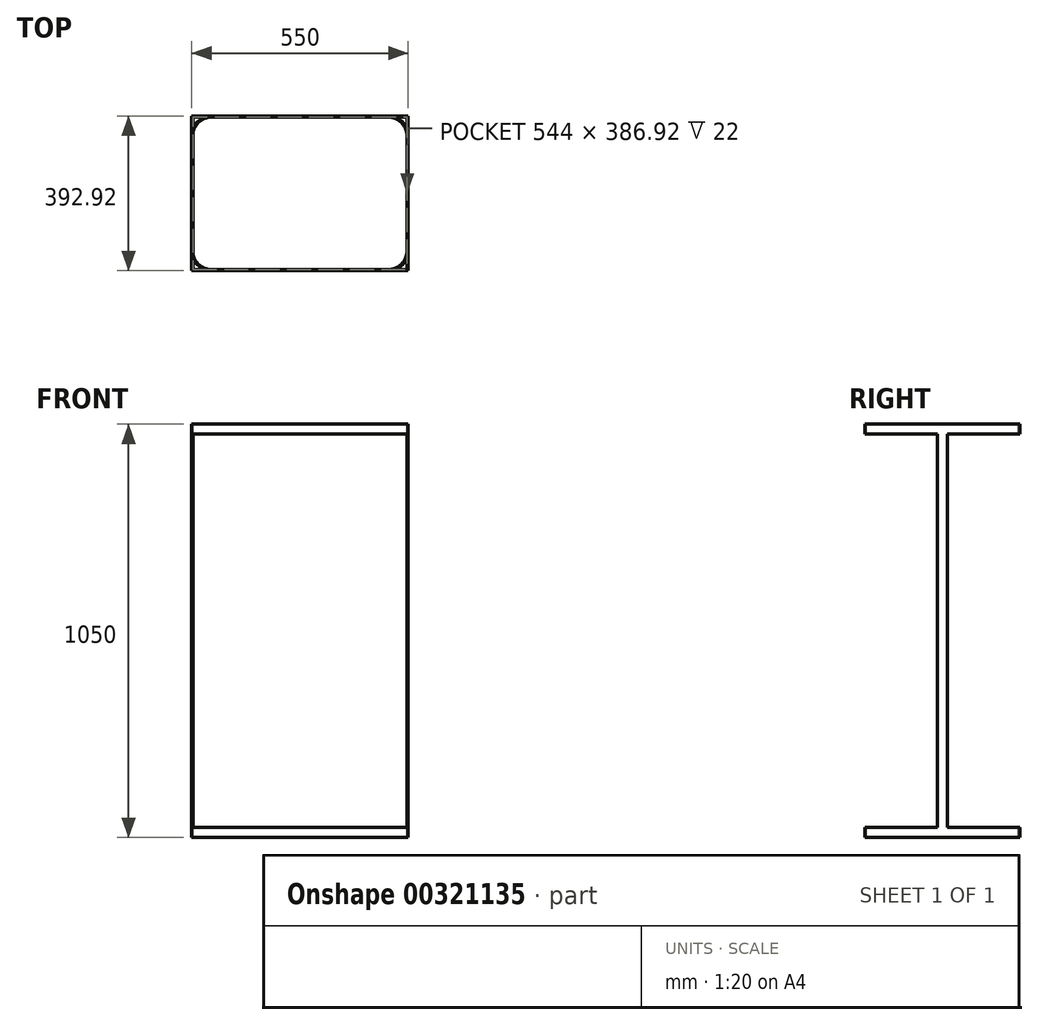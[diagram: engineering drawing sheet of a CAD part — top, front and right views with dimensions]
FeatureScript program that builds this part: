
annotation { "Feature Type Name" : "Feature", "Feature Type Description" : "" }
export const myFeature = defineFeature(function(context is Context, id is Id, definition is map)
    precondition{}
    {
        {
            var Q0;
            Q0=qCreatedBy(makeId("Top.planeOp"),FACE);
            var sketch = newSketch(context, id + "F0", { "sketchPlane" : qUnion([Q0])});
            skLineSegment(sketch, "E0", {"start": v(-225, -20) * mm, "end": v(225, -20) * mm});
            skLineSegment(sketch, "E1", {"start": v(-225, -412.92) * mm, "end": v(225, -412.92) * mm});
            skLineSegment(sketch, "E2", {"start": v(275, -70) * mm, "end": v(275, -362.92) * mm});
            skLineSegment(sketch, "E3", {"start": v(-275, -70) * mm, "end": v(-275, -362.92) * mm});
            skArc(sketch, "E4", {"start": v(-225, -20) * mm, "mid": v(-260.36, -34.64) * mm, "end": v(-275, -70) * mm});
            skArc(sketch, "E5", {"start": v(-275, -362.92) * mm, "mid": v(-260.36, -398.28) * mm, "end": v(-225, -412.92) * mm});
            skArc(sketch, "E6", {"start": v(225, -412.92) * mm, "mid": v(260.36, -398.28) * mm, "end": v(275, -362.92) * mm});
            skArc(sketch, "E7", {"start": v(275, -70) * mm, "mid": v(260.36, -34.64) * mm, "end": v(225, -20) * mm});
            skArc(sketch, "E8.0", {"start": v(-225, -23) * mm, "mid": v(-258.23, -36.77) * mm, "end": v(-272, -70) * mm});
            skLineSegment(sketch, "E8.1", {"start": v(-272, -70) * mm, "end": v(-272, -362.92) * mm});
            skLineSegment(sketch, "E8.2", {"start": v(-225, -23) * mm, "end": v(225, -23) * mm});
            skArc(sketch, "E8.3", {"start": v(-272, -362.92) * mm, "mid": v(-258.23, -396.15) * mm, "end": v(-225, -409.92) * mm});
            skArc(sketch, "E8.4", {"start": v(272, -70) * mm, "mid": v(258.23, -36.77) * mm, "end": v(225, -23) * mm});
            skLineSegment(sketch, "E8.5", {"start": v(272, -70) * mm, "end": v(272, -362.92) * mm});
            skArc(sketch, "E8.6", {"start": v(225, -409.92) * mm, "mid": v(258.23, -396.15) * mm, "end": v(272, -362.92) * mm});
            skLineSegment(sketch, "E8.7", {"start": v(-225, -409.92) * mm, "end": v(225, -409.92) * mm});
            skSolve(sketch);
        }
        {
            var Q0;
            Q0 = qSketchRegion(id + "F0", true);
            extrude(context, id + "F1", {"entities" : qUnion([Q0]), "oppositeDirection" : true, "depth" : 25 * mm});
        }
        {
            var Q0;
            Q0=makeQuery(id+"F1.opExtrude","SWEPT_FACE",FACE,{"disambiguationData":[OSD([sQuery(id+"F0.wireOp",EDGE,"E2")])]});
            var sketch = newSketch(context, id + "F2", { "sketchPlane" : qUnion([Q0])});
            skLineSegment(sketch, "E9.bottom", {"start": v(-228.96, -25) * mm, "end": v(-203.96, -25) * mm});
            skLineSegment(sketch, "E9.top", {"start": v(-228.96, -1025) * mm, "end": v(-203.96, -1025) * mm});
            skLineSegment(sketch, "E9.left", {"start": v(-228.96, -25) * mm, "end": v(-228.96, -1025) * mm});
            skLineSegment(sketch, "E9.right", {"start": v(-203.96, -25) * mm, "end": v(-203.96, -1025) * mm});
            skSolve(sketch);
        }
        {
            var Q0;
            Q0 = qSketchRegion(id + "F2", true);
            extrude(context, id + "F3", {"entities" : qUnion([Q0]), "oppositeDirection" : true, "depth" : 3 * mm, "offsetDistance" : 25 * mm});
        }
        {
            var Q0;
            Q0=makeQuery(id+"F3.opExtrude","SWEPT_BODY",BODY,{"disambiguationData":[OSD([sQuery(id+"F2.wireOp",EDGE,"E9.bottom"),sQuery(id+"F2.wireOp",EDGE,"E9.top"),sQuery(id+"F2.wireOp",EDGE,"E9.left"),sQuery(id+"F2.wireOp",EDGE,"E9.right")])]});
            var Q1;
            Q1=qCreatedBy(makeId("Right.planeOp"),FACE);
            mirror(context, id + "F4", {"operationType" : NewBodyOperationType.ADD, "entities" : qUnion([Q0]), "mirrorPlane" : qUnion([Q1])});
        }
        {
            var Q0;
            Q0=makeQuery(id+"F4.opPattern","COPY",FACE,{"derivedFrom":makeQuery(id+"F3.opExtrude","SWEPT_FACE",FACE,{"disambiguationData":[OSD([sQuery(id+"F2.wireOp",EDGE,"E9.top")])]}),"instanceName":"1"});
            var sketch = newSketch(context, id + "F5", { "sketchPlane" : qUnion([Q0])});
            skLineSegment(sketch, "E10.bottom", {"start": v(-275, 412.92) * mm, "end": v(275, 412.92) * mm});
            skLineSegment(sketch, "E10.top", {"start": v(-275, 20) * mm, "end": v(275, 20) * mm});
            skLineSegment(sketch, "E10.left", {"start": v(-275, 412.92) * mm, "end": v(-275, 20) * mm});
            skLineSegment(sketch, "E10.right", {"start": v(275, 412.92) * mm, "end": v(275, 20) * mm});
            skPoint(sketch, "E10.middle", {"position": v(0, 216.46) * mm});
            skSolve(sketch);
        }
        {
            var Q0;
            Q0 = qSketchRegion(id + "F5", true);
            extrude(context, id + "F6", {"entities" : qUnion([Q0]), "operationType" : NewBodyOperationType.ADD, "depth" : 25 * mm, "offsetDistance" : 25 * mm});
        }
        {
            var Q0;
            Q0=makeQuery(id+"F6.opExtrude","CAP_FACE",FACE,{"disambiguationData":[OSD([sQuery(id+"F5.wireOp",EDGE,"E10.bottom"),sQuery(id+"F5.wireOp",EDGE,"E10.top"),sQuery(id+"F5.wireOp",EDGE,"E10.left"),sQuery(id+"F5.wireOp",EDGE,"E10.right")])],"isStart":true});
            shell(context, id + "F7", {"entities" : qUnion([Q0]), "thickness" : 3 * mm});
        }
    });
